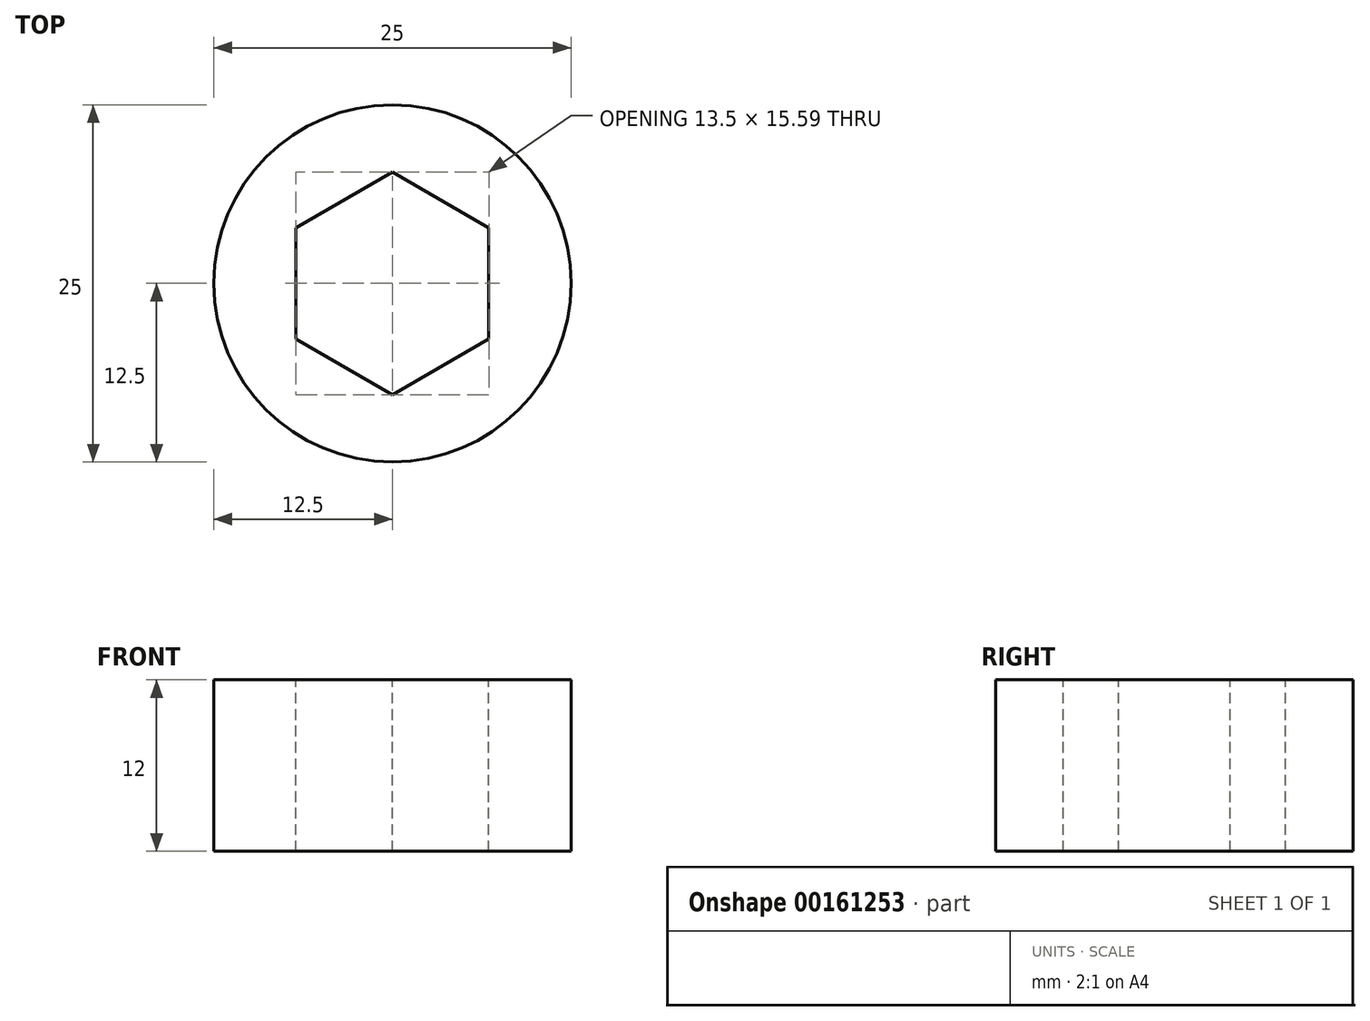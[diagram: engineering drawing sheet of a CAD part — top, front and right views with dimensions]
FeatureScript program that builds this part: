
annotation { "Feature Type Name" : "Feature", "Feature Type Description" : "" }
export const myFeature = defineFeature(function(context is Context, id is Id, definition is map)
    precondition{}
    {
        {
            assignVariable(context, id + "F0", {"name" : "offset", "anyValue" : .4});
        }
        {
            var Q0;
            Q0=qCreatedBy(makeId("Top.planeOp"),FACE);
            var sketch = newSketch(context, id + "F1", { "sketchPlane" : qUnion([Q0])});
            skCircle(sketch, "E0", {"center": v(0, 0) * mm, "radius": 12.5 * mm});
            skSolve(sketch);
        }
        {
            var Q0;
            Q0=makeQuery(id+"F1.imprint","IMPRINT",FACE,{"disambiguationData":[TD([[makeQuery(id+"F1.imprint","IMPRINT",EDGE,{"derivedFrom":sQuery(id+"F1.wireOp",EDGE,"E0")}),1.0]])]});
            extrude(context, id + "F2", {"entities" : qUnion([Q0]), "depth" : 12 * mm});
        }
        {
            var Q0;
            Q0=makeQuery(id+"F2.opExtrude","CAP_FACE",FACE,{"disambiguationData":[OSD([sQuery(id+"F1.wireOp",EDGE,"E0")])],"isStart":false});
            var sketch = newSketch(context, id + "F3", { "sketchPlane" : qUnion([Q0])});
            skCircle(sketch, "E1.cCircle", {"center": v(0, 0) * mm, "radius": 6.35 * mm, "construction": true});
            skLineSegment(sketch, "E1.0", {"start": v(6.35, -3.67) * mm, "end": v(0, -7.33) * mm});
            skLineSegment(sketch, "E1.1", {"start": v(0, -7.33) * mm, "end": v(-6.35, -3.67) * mm});
            skLineSegment(sketch, "E1.2", {"start": v(-6.35, -3.67) * mm, "end": v(-6.35, 3.67) * mm});
            skLineSegment(sketch, "E1.3", {"start": v(-6.35, 3.67) * mm, "end": v(0, 7.33) * mm});
            skLineSegment(sketch, "E1.4", {"start": v(0, 7.33) * mm, "end": v(6.35, 3.67) * mm});
            skLineSegment(sketch, "E1.5", {"start": v(6.35, 3.67) * mm, "end": v(6.35, -3.67) * mm});
            skPoint(sketch, "E1.0.midPoint", {"position": v(3.17, -5.5) * mm});
            skSolve(sketch);
        }
        {
            var Q0;
            Q0=makeQuery(id+"F3.imprint","IMPRINT",FACE,{"disambiguationData":[TD([[makeQuery(id+"F3.imprint","IMPRINT",EDGE,{"derivedFrom":sQuery(id+"F3.wireOp",EDGE,"E1.0")}),-1.0]])]});
            extrude(context, id + "F4", {"entities" : qUnion([Q0]), "oppositeDirection" : true, "depth" : 25 * mm, "hasSecondDirection" : true, "secondDirectionOppositeDirection" : false, "secondDirectionDepth" : 25 * mm});
        }
        {
            var Q0;
            Q0=makeQuery(id+"F4.opExtrude","SWEPT_BODY",BODY,{"disambiguationData":[OSD([sQuery(id+"F3.wireOp",EDGE,"E1.0"),sQuery(id+"F3.wireOp",EDGE,"E1.1"),sQuery(id+"F3.wireOp",EDGE,"E1.2"),sQuery(id+"F3.wireOp",EDGE,"E1.3"),sQuery(id+"F3.wireOp",EDGE,"E1.4"),sQuery(id+"F3.wireOp",EDGE,"E1.5")])]});
            var Q1;
            Q1=makeQuery(id+"F2.opExtrude","SWEPT_BODY",BODY,{"disambiguationData":[OSD([sQuery(id+"F1.wireOp",EDGE,"E0")])]});
            booleanBodies(context, id + "F5", {"operationType" : BooleanOperationType.SUBTRACTION, "tools" : qUnion([Q0]), "targets" : qUnion([Q1]), "offset" : true, "offsetAll" : true, "offsetDistance" : (getVariable(context, 'offset')) * mm});
        }
    });
